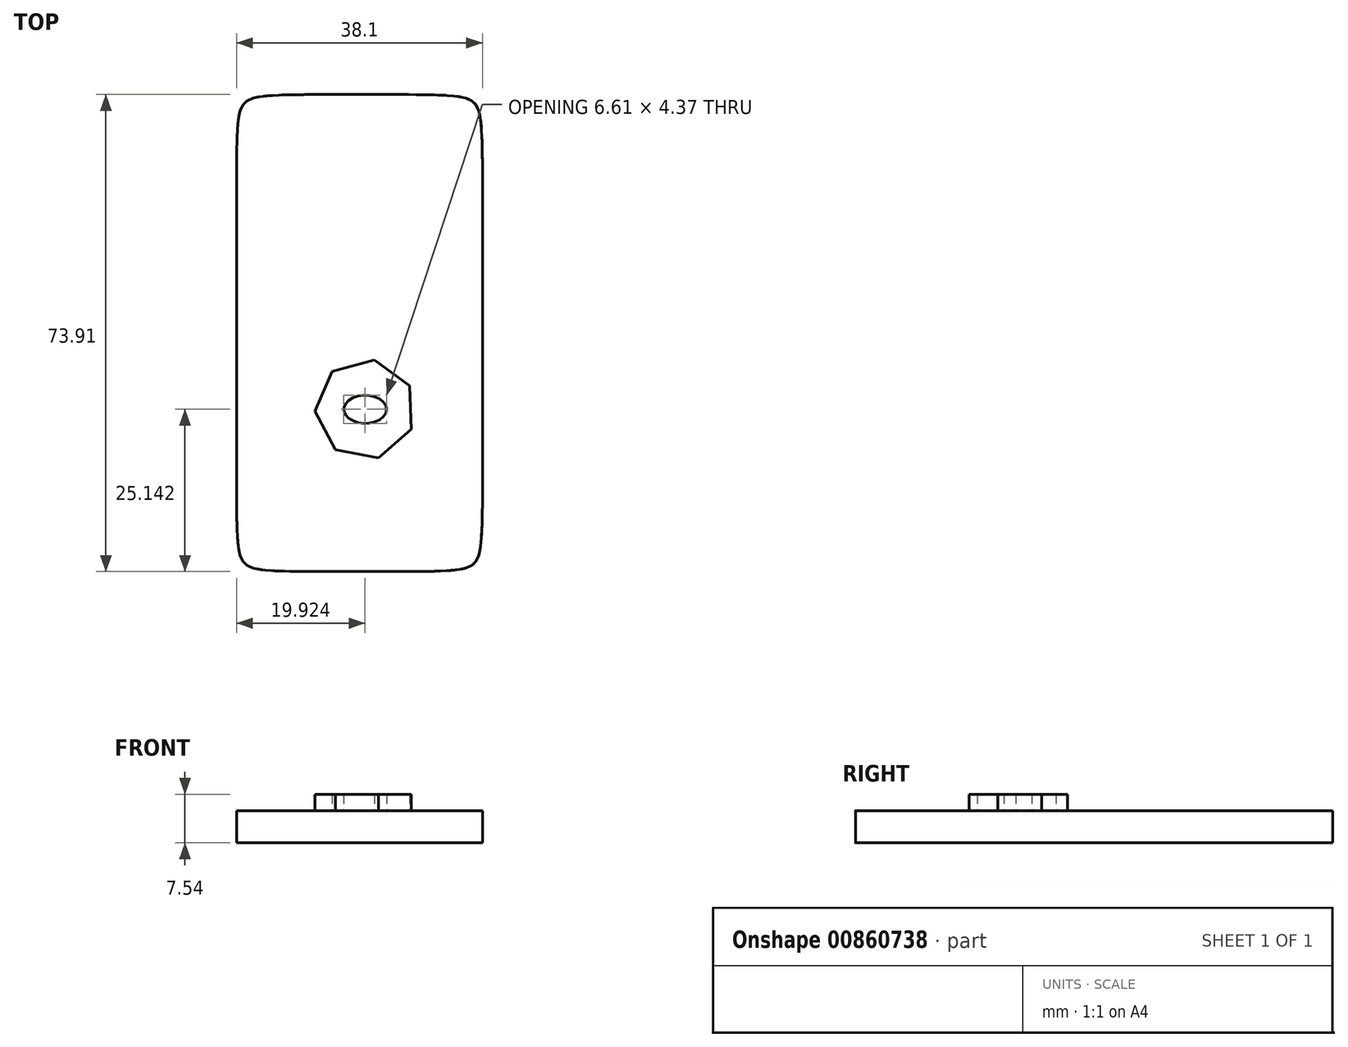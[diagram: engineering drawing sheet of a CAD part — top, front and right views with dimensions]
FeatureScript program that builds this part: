
annotation { "Feature Type Name" : "Feature", "Feature Type Description" : "" }
export const myFeature = defineFeature(function(context is Context, id is Id, definition is map)
    precondition{}
    {
        {
            var Q0;
            Q0=qCreatedBy(makeId("Front.planeOp"),FACE);
            var sketch = newSketch(context, id + "F0", { "sketchPlane" : qUnion([Q0])});
            skLineSegment(sketch, "E0.bottom", {"start": v(0, 0) * mm, "end": v(38.1, 0) * mm});
            skLineSegment(sketch, "E0.top", {"start": v(0, 5) * mm, "end": v(38.1, 5) * mm});
            skLineSegment(sketch, "E0.left", {"start": v(0, 0) * mm, "end": v(0, 5) * mm});
            skLineSegment(sketch, "E0.right", {"start": v(38.1, 0) * mm, "end": v(38.1, 5) * mm});
            skSolve(sketch);
        }
        {
            var Q0;
            Q0 = qSketchRegion(id + "F0", true);
            extrude(context, id + "F1", {"entities" : qUnion([Q0]), "depth" : 73.9 * mm, "offsetDistance" : 25.4 * mm});
        }
        {
            var Q0;
            Q0=makeQuery(id+"F1.opExtrude","CAP_EDGE",EDGE,{"disambiguationData":[OSD([sQuery(id+"F0.wireOp",EDGE,"E0.right")])],"isStart":false});
            var Q1;
            Q1=makeQuery(id+"F1.opExtrude","CAP_EDGE",EDGE,{"disambiguationData":[OSD([sQuery(id+"F0.wireOp",EDGE,"E0.left")])],"isStart":true});
            var Q2;
            Q2=makeQuery(id+"F1.opExtrude","CAP_EDGE",EDGE,{"disambiguationData":[OSD([sQuery(id+"F0.wireOp",EDGE,"E0.right")])],"isStart":true});
            var Q3;
            Q3=makeQuery(id+"F1.opExtrude","CAP_EDGE",EDGE,{"disambiguationData":[OSD([sQuery(id+"F0.wireOp",EDGE,"E0.left")])],"isStart":false});
            fillet(context, id + "F2", {"entities" : qUnion([Q0, Q1, Q2, Q3]), "radius" : 12.7 * mm, "tangentPropagation" : true, "rho" : .8, "crossSection" : FilletCrossSection.CONIC, "allowEdgeOverflow" : false});
        }
        {
            var Q0;
            Q0=makeQuery(id+"F1.opExtrude","SWEPT_FACE",FACE,{"disambiguationData":[OSD([sQuery(id+"F0.wireOp",EDGE,"E0.top")])]});
            var sketch = newSketch(context, id + "F3", { "sketchPlane" : qUnion([Q0])});
            skEllipse(sketch, "E1", {"center": v(19.92, -48.77) * mm, "majorRadius": 3.3 * mm, "minorRadius": 2.18 * mm, "majorAxis": v(1, 0)});
            skSolve(sketch);
        }
        {
            var Q0;
            Q0=makeQuery(id+"F1.opExtrude","SWEPT_FACE",FACE,{"disambiguationData":[OSD([sQuery(id+"F0.wireOp",EDGE,"E0.top")])]});
            var sketch = newSketch(context, id + "F4", { "sketchPlane" : qUnion([Q0])});
            skEllipse(sketch, "E2.0", {"center": v(19.92, -48.77) * mm, "majorRadius": 3.3 * mm, "minorRadius": 2.18 * mm, "majorAxis": v(1, 0)});
            skCircle(sketch, "E3.cCircle", {"center": v(19.92, -48.77) * mm, "radius": 7.02 * mm, "construction": true});
            skLineSegment(sketch, "E3.0", {"start": v(27.08, -51.87) * mm, "end": v(21.96, -56.3) * mm});
            skLineSegment(sketch, "E3.1", {"start": v(21.96, -56.3) * mm, "end": v(15.31, -55.05) * mm});
            skLineSegment(sketch, "E3.2", {"start": v(15.31, -55.05) * mm, "end": v(12.14, -49.08) * mm});
            skLineSegment(sketch, "E3.3", {"start": v(12.14, -49.08) * mm, "end": v(14.83, -42.87) * mm});
            skLineSegment(sketch, "E3.4", {"start": v(14.83, -42.87) * mm, "end": v(21.36, -41.1) * mm});
            skLineSegment(sketch, "E3.5", {"start": v(21.36, -41.1) * mm, "end": v(26.8, -45.1) * mm});
            skLineSegment(sketch, "E3.6", {"start": v(26.8, -45.1) * mm, "end": v(27.08, -51.87) * mm});
            skPoint(sketch, "E3.0.midPoint", {"position": v(24.52, -54.08) * mm});
            skSolve(sketch);
        }
        {
            var Q0;
            Q0=makeQuery(id+"F4.imprint","IMPRINT",FACE,{"disambiguationData":[TD([[makeQuery(id+"F4.imprint","IMPRINT",EDGE,{"derivedFrom":sQuery(id+"F4.wireOp",EDGE,"E2.0")}),-1.0]])]});
            extrude(context, id + "F5", {"entities" : qUnion([Q0]), "depth" : 2.54 * mm, "offsetDistance" : 25.4 * mm});
        }
    });
